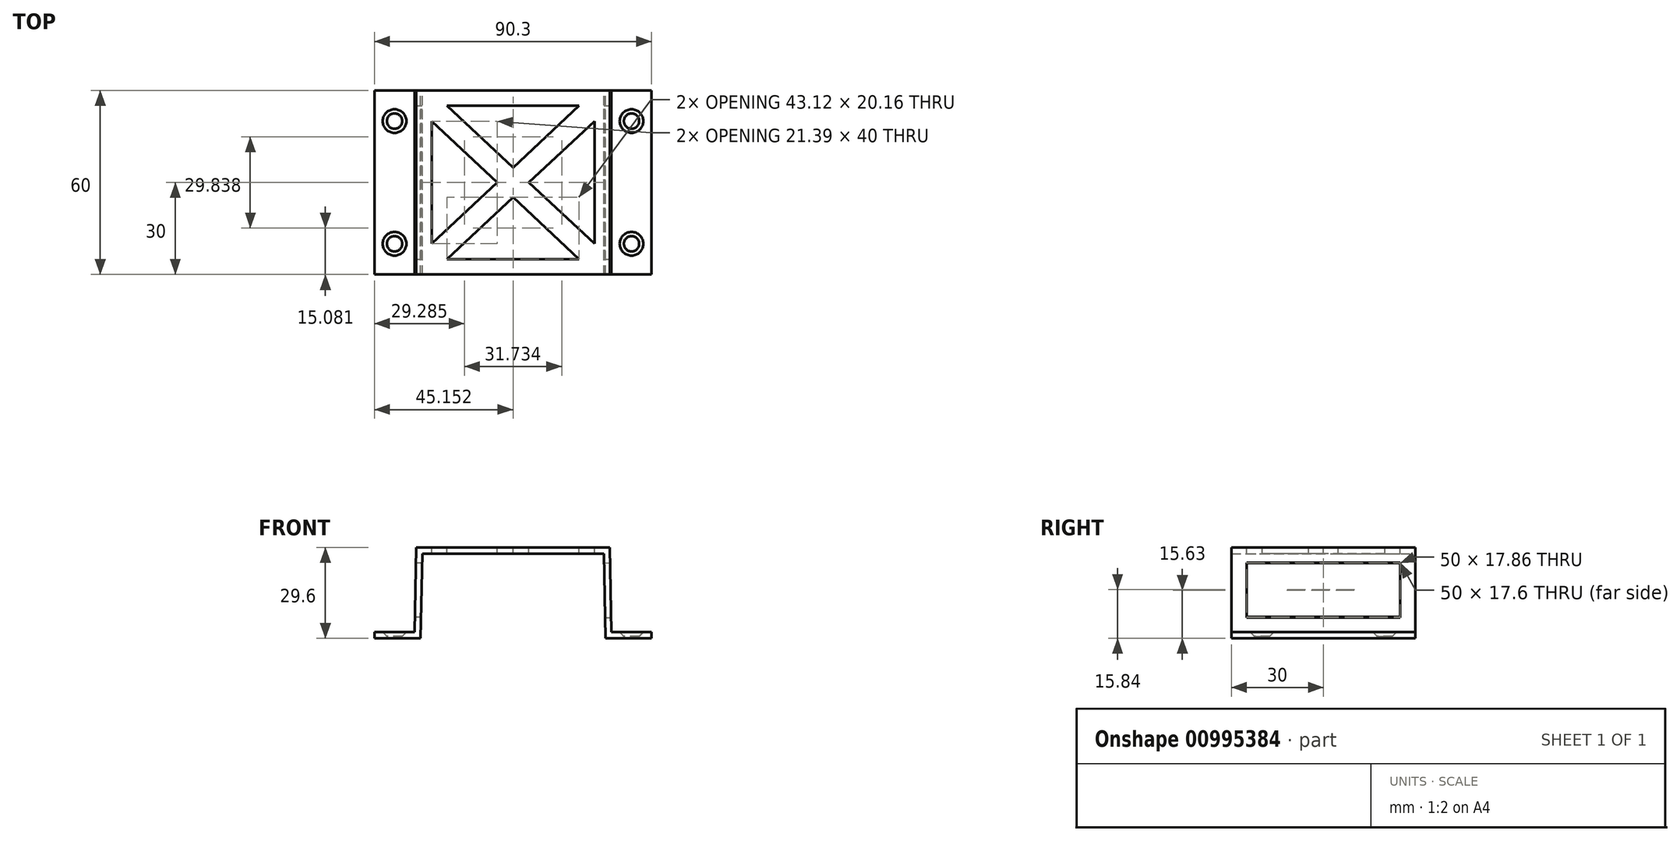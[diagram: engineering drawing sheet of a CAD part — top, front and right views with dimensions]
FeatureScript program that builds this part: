
annotation { "Feature Type Name" : "Feature", "Feature Type Description" : "" }
export const myFeature = defineFeature(function(context is Context, id is Id, definition is map)
    precondition{}
    {
        {
            var Q0;
            Q0=qCreatedBy(makeId("Front.planeOp"),FACE);
            var sketch = newSketch(context, id + "F0", { "sketchPlane" : qUnion([Q0])});
            skLineSegment(sketch, "E0", {"start": v(-88.33, 13.4) * mm, "end": v(-73.33, 13.4) * mm});
            skLineSegment(sketch, "E1", {"start": v(-73.33, 13.4) * mm, "end": v(-72.78, 41) * mm});
            skLineSegment(sketch, "E2", {"start": v(-72.78, 41) * mm, "end": v(-13.58, 41) * mm});
            skLineSegment(sketch, "E3", {"start": v(-13.58, 41) * mm, "end": v(-13.03, 13.4) * mm});
            skLineSegment(sketch, "E4", {"start": v(-13.03, 13.4) * mm, "end": v(1.97, 13.4) * mm});
            skPoint(sketch, "E5", {"position": v(-43.18, 41) * mm});
            skLineSegment(sketch, "E6", {"start": v(-73.33, 13.4) * mm, "end": v(-13.03, 13.4) * mm, "construction": true});
            skPoint(sketch, "E7", {"position": v(-43.18, 13.4) * mm});
            skLineSegment(sketch, "E8.0", {"start": v(-11.07, 15.4) * mm, "end": v(1.97, 15.4) * mm});
            skLineSegment(sketch, "E8.1", {"start": v(-88.33, 15.4) * mm, "end": v(-75.29, 15.4) * mm});
            skLineSegment(sketch, "E8.2", {"start": v(-75.29, 15.4) * mm, "end": v(-74.74, 43) * mm});
            skLineSegment(sketch, "E8.3", {"start": v(-74.74, 43) * mm, "end": v(-11.62, 43) * mm});
            skLineSegment(sketch, "E8.4", {"start": v(-11.62, 43) * mm, "end": v(-11.07, 15.4) * mm});
            skLineSegment(sketch, "E9", {"start": v(-88.33, 13.4) * mm, "end": v(-88.33, 15.4) * mm});
            skLineSegment(sketch, "E10", {"start": v(1.97, 15.4) * mm, "end": v(1.97, 13.4) * mm});
            skSolve(sketch);
        }
        {
            var Q0;
            Q0 = qSketchRegion(id + "F0", true);
            extrude(context, id + "F1", {"entities" : qUnion([Q0]), "depth" : 60 * mm, "offsetDistance" : 25 * mm});
        }
        {
            var Q0;
            Q0=makeQuery(id+"F1.opExtrude","SWEPT_FACE",FACE,{"disambiguationData":[OSD([sQuery(id+"F0.wireOp",EDGE,"E8.0")])]});
            var sketch = newSketch(context, id + "F2", { "sketchPlane" : qUnion([Q0])});
            skLineSegment(sketch, "E11.0.0", {"start": v(-75.29, 0) * mm, "end": v(-88.33, 0) * mm, "construction": true});
            skLineSegment(sketch, "E11.0.1", {"start": v(-88.33, 0) * mm, "end": v(-88.33, -60) * mm, "construction": true});
            skLineSegment(sketch, "E11.0.2", {"start": v(-88.33, -60) * mm, "end": v(-75.29, -60) * mm, "construction": true});
            skLineSegment(sketch, "E11.0.3", {"start": v(-75.29, -60) * mm, "end": v(-75.29, 0) * mm, "construction": true});
            skLineSegment(sketch, "E12.0.0", {"start": v(1.97, 0) * mm, "end": v(-11.07, 0) * mm, "construction": true});
            skLineSegment(sketch, "E12.0.1", {"start": v(-11.07, 0) * mm, "end": v(-11.07, -60) * mm, "construction": true});
            skLineSegment(sketch, "E12.0.2", {"start": v(-11.07, -60) * mm, "end": v(1.97, -60) * mm, "construction": true});
            skLineSegment(sketch, "E12.0.3", {"start": v(1.97, -60) * mm, "end": v(1.97, 0) * mm, "construction": true});
            skLineSegment(sketch, "E13", {"start": v(-81.8, 0) * mm, "end": v(-81.8, -60) * mm, "construction": true});
            skLineSegment(sketch, "E14", {"start": v(-4.55, 0) * mm, "end": v(-4.55, -60) * mm, "construction": true});
            skLineSegment(sketch, "E15", {"start": v(-88.33, -10) * mm, "end": v(1.97, -10) * mm, "construction": true});
            skLineSegment(sketch, "E16", {"start": v(-88.33, -50) * mm, "end": v(1.97, -50) * mm, "construction": true});
            skCircle(sketch, "E17", {"center": v(-81.8, -10) * mm, "radius": 3.85 * mm});
            skCircle(sketch, "E18", {"center": v(-4.55, -10) * mm, "radius": 3.85 * mm});
            skCircle(sketch, "E19", {"center": v(-4.55, -50) * mm, "radius": 3.85 * mm});
            skCircle(sketch, "E20", {"center": v(-81.8, -50) * mm, "radius": 3.85 * mm});
            skSolve(sketch);
        }
        {
            var Q0;
            Q0=sQuery(id+"F2.wireOp",VERTEX,"E17.center");
            var Q1;
            Q1=sQuery(id+"F2.wireOp",VERTEX,"E20.center");
            var Q2;
            Q2=sQuery(id+"F2.wireOp",VERTEX,"E19.center");
            var Q3;
            Q3=sQuery(id+"F2.wireOp",VERTEX,"E18.center");
            var Q4;
            Q4=makeQuery(id+"F1.opExtrude","SWEPT_BODY",BODY,{"disambiguationData":[OSD([sQuery(id+"F0.wireOp",EDGE,"E0"),sQuery(id+"F0.wireOp",EDGE,"E1"),sQuery(id+"F0.wireOp",EDGE,"E2"),sQuery(id+"F0.wireOp",EDGE,"E3"),sQuery(id+"F0.wireOp",EDGE,"E4"),sQuery(id+"F0.wireOp",EDGE,"E8.0"),sQuery(id+"F0.wireOp",EDGE,"E8.1"),sQuery(id+"F0.wireOp",EDGE,"E8.2"),sQuery(id+"F0.wireOp",EDGE,"E8.3"),sQuery(id+"F0.wireOp",EDGE,"E8.4"),sQuery(id+"F0.wireOp",EDGE,"E9"),sQuery(id+"F0.wireOp",EDGE,"E10")])]});
            hole(context, id + "F3", {"style" : HoleStyle.C_SINK, "endStyle" : HoleEndStyle.THROUGH, "holeDiameter" : 5 * mm, "cSinkDiameter" : 7.7 * mm, "cSinkAngle" : 90 * degree, "majorDiameter" : 5 * mm, "isTappedThrough" : true, "tappedDepth" : 12 * mm, "tapClearance" : 3, "locations" : qUnion([Q0, Q1, Q2, Q3]), "scope" : qUnion([Q4])});
        }
        {
            var Q0;
            Q0=makeQuery(id+"F1.opExtrude","SWEPT_FACE",FACE,{"disambiguationData":[OSD([sQuery(id+"F0.wireOp",EDGE,"E8.3")])]});
            var sketch = newSketch(context, id + "F4", { "sketchPlane" : qUnion([Q0])});
            skLineSegment(sketch, "E21.bottom", {"start": v(-64.74, -5) * mm, "end": v(-21.62, -5) * mm});
            skLineSegment(sketch, "E21.top", {"start": v(-64.74, -55) * mm, "end": v(-21.62, -55) * mm});
            skLineSegment(sketch, "E21.left", {"start": v(-69.74, -10) * mm, "end": v(-69.74, -50) * mm});
            skLineSegment(sketch, "E21.right", {"start": v(-16.62, -10) * mm, "end": v(-16.62, -50) * mm});
            skLineSegment(sketch, "E22", {"start": v(-69.74, -10) * mm, "end": v(-48.35, -30) * mm});
            skLineSegment(sketch, "E23", {"start": v(-16.62, -50) * mm, "end": v(-38, -30) * mm});
            skLineSegment(sketch, "E24", {"start": v(-21.62, -5) * mm, "end": v(-43.18, -25.16) * mm});
            skLineSegment(sketch, "E25", {"start": v(-64.74, -55) * mm, "end": v(-43.18, -34.84) * mm});
            skLineSegment(sketch, "E26.trimOffspring", {"start": v(-38, -30) * mm, "end": v(-16.62, -10) * mm});
            skLineSegment(sketch, "E27.trimOffspring", {"start": v(-43.18, -25.16) * mm, "end": v(-64.74, -5) * mm});
            skLineSegment(sketch, "E28.trimOffspring", {"start": v(-48.35, -30) * mm, "end": v(-69.74, -50) * mm});
            skLineSegment(sketch, "E29.trimOffspring", {"start": v(-43.18, -34.84) * mm, "end": v(-21.62, -55) * mm});
            skSolve(sketch);
        }
        {
            var Q0;
            Q0=makeQuery(id+"F4.imprint","IMPRINT",FACE,{"disambiguationData":[TD([[makeQuery(id+"F4.imprint","IMPRINT",EDGE,{"derivedFrom":sQuery(id+"F4.wireOp",EDGE,"E21.left")}),1.0]])]});
            var Q1;
            Q1=makeQuery(id+"F4.imprint","IMPRINT",FACE,{"disambiguationData":[TD([[makeQuery(id+"F4.imprint","IMPRINT",EDGE,{"derivedFrom":sQuery(id+"F4.wireOp",EDGE,"E21.bottom")}),-1.0]])]});
            var Q2;
            Q2=makeQuery(id+"F4.imprint","IMPRINT",FACE,{"disambiguationData":[TD([[makeQuery(id+"F4.imprint","IMPRINT",EDGE,{"derivedFrom":sQuery(id+"F4.wireOp",EDGE,"E21.right")}),-1.0]])]});
            var Q3;
            Q3=makeQuery(id+"F4.imprint","IMPRINT",FACE,{"disambiguationData":[TD([[makeQuery(id+"F4.imprint","IMPRINT",EDGE,{"derivedFrom":sQuery(id+"F4.wireOp",EDGE,"E21.top")}),1.0]])]});
            extrude(context, id + "F5", {"entities" : qUnion([Q0, Q1, Q2, Q3]), "operationType" : NewBodyOperationType.REMOVE, "endBound" : BoundingType.THROUGH_ALL, "oppositeDirection" : true, "depth" : 25 * mm, "offsetDistance" : 25 * mm});
        }
        {
            var Q0;
            Q0=makeQuery(id+"F1.opExtrude","SWEPT_FACE",FACE,{"disambiguationData":[OSD([sQuery(id+"F0.wireOp",EDGE,"E8.4")])]});
            var sketch = newSketch(context, id + "F6", { "sketchPlane" : qUnion([Q0])});
            skLineSegment(sketch, "E30.bottom", {"start": v(-55, 38.22) * mm, "end": v(-5, 38.22) * mm});
            skLineSegment(sketch, "E30.top", {"start": v(-55, 20.36) * mm, "end": v(-5, 20.36) * mm});
            skLineSegment(sketch, "E30.left", {"start": v(-55, 38.22) * mm, "end": v(-55, 20.36) * mm});
            skLineSegment(sketch, "E30.right", {"start": v(-5, 38.22) * mm, "end": v(-5, 20.36) * mm});
            skSolve(sketch);
        }
        {
            var Q0;
            Q0=makeQuery(id+"F1.opExtrude","SWEPT_FACE",FACE,{"disambiguationData":[OSD([sQuery(id+"F0.wireOp",EDGE,"E8.2")])]});
            var sketch = newSketch(context, id + "F7", { "sketchPlane" : qUnion([Q0])});
            skLineSegment(sketch, "E31.bottom", {"start": v(5, 36.5) * mm, "end": v(55, 36.5) * mm});
            skLineSegment(sketch, "E31.top", {"start": v(5, 18.9) * mm, "end": v(55, 18.9) * mm});
            skLineSegment(sketch, "E31.left", {"start": v(5, 36.5) * mm, "end": v(5, 18.9) * mm});
            skLineSegment(sketch, "E31.right", {"start": v(55, 36.5) * mm, "end": v(55, 18.9) * mm});
            skSolve(sketch);
        }
        {
            var Q0;
            Q0=makeQuery(id+"F6.imprint","IMPRINT",FACE,{"disambiguationData":[TD([[makeQuery(id+"F6.imprint","IMPRINT",EDGE,{"derivedFrom":sQuery(id+"F6.wireOp",EDGE,"E30.bottom")}),-1.0]])]});
            var Q1;
            Q1=makeQuery(id+"F7.imprint","IMPRINT",FACE,{"disambiguationData":[TD([[makeQuery(id+"F7.imprint","IMPRINT",EDGE,{"derivedFrom":sQuery(id+"F7.wireOp",EDGE,"E31.bottom")}),-1.0]])]});
            extrude(context, id + "F8", {"entities" : qUnion([Q0, Q1]), "operationType" : NewBodyOperationType.REMOVE, "endBound" : BoundingType.SYMMETRIC, "oppositeDirection" : true, "depth" : 10 * mm, "offsetDistance" : 25 * mm});
        }
    });
